# Revit family: Legrand_Bornes_recharge_vehicules_electriques_Green_up_Metal_bornes_recharge_connectees
name_source: partatom
category: Equipement électrique
units: mm (PartAtom-declared; Revit-internal decimal feet)

## family parameters
Basée sur le plan de construction = Non
Configuration du panneau = Deux colonnes, circuits au sein
Cote de connecteur circulaire = Utiliser le diamètre
Couper avec des vides une fois chargée = Non
Numéro OmniClass = 23.80.30.11.17
Partagée = Non
Point de calcul de pièce = Non
Titre OmniClass = Distribution Boards and Control Panels
Toujours verticalement = Oui
Type d'élément = Tableau de raccordement

## types (20) — shared parameters
ETIM Class 6.0 = EC002883
Fabricant = Legrand
IK = 08
IP = 44
Modèle = Borne Métal Green'up Legrand
Tension = 220
URL = www.legrand.fr
déclencheur émission signal de sécurité = 406276
zero-valued in all types: Elévation par défaut

## per-type parameters (varying)
| type | Conditions Générale d'Utilisation | Description | Image du type | Puissance | borne fixation murale | borne sur pied | différentiel | disjoncteur Protection ligne 2P+T (minimum) | disjoncteur différentiel Protection ligne Type 2S | intensité Protection ligne 2P+T | intensité Protection ligne Type 2S | intensité borne | interrupteur différentiel | réglage puissance | section ligne 2P+T  (minimum) | section ligne Type 2S (minimum) |
| Borne Green'up murale Premium monophasée Métal - Mode 3 - 7,4kW - 32A 1 véhicule | https://export.legrand.com | 059004  Borne Green'up murale Premium monophasée Métal - Mode 3 - 7,4kW - 32A 1 véhicule | Borne_ve_metal_murale_059011.jpg | 7.4 | Oui | Non | 30 mA type F (ex Hpi) | 406884 (4500/6 kA) | 410859 (4500/6 kA) | 20 A courbe C | 40 A courbe C | 16 A |  | 7400 W | 3 mm  [stored 0.00984252 ft] | 10 mm  [stored 0.0328084 ft] |
| Borne Green'up murale Premium monophasée Métal - Mode 3 - 4,6kW - 20A 1 véhicule | https://export.legrand.com | 059003  Borne Green'up murale Premium monophasée Métal - Mode 3 - 4,6kW - 20A 1 véhicule | Borne_ve_metal_murale_059011.jpg | 4.6 | Oui | Non | 30 mA type F (ex Hpi) | 406884 (4500/6 kA) | 410755 (4500/6 kA) | 20 A courbe C | 25 A courbe C | 20 A |  | 4600 W | 3 mm  [stored 0.00984252 ft] | 4 mm  [stored 0.0131234 ft] |
| Borne Green'up murale Premium monophasée Métal -  Mode 3 - 3,7kW - 16A 1 véhicule | https://export.legrand.com | 059003  Borne Green'up murale Premium monophasée Métal -  Mode 3 - 3,7kW - 16A 1 véhicule | Borne_ve_metal_murale_059011.jpg | 3.7 | Oui | Non | 30 mA type F (ex Hpi) |  | 410754 (4500/6 kA) |  | 20 A courbe C | 16 A |  | 3700 W | 0 mm  [stored 0 ft] | 3 mm  [stored 0.00984252 ft] |
| Borne Green'up murale Premium triphasée Métal - Mode 3 - 22kW - 32A 1 véhicule | https://export.legrand.com | 059014  Borne Green'up murale Premium triphasée Métal - Mode 3 - 22kW - 32A 1 véhicule | Borne_ve_metal_murale_059011.jpg | 22 | Oui | Non | 30 mA type B | 406884 (4500/6 kA) | 407902 (6000/10 kA) | 20 A courbe C | 40 A courbe C | 32 A | 411846 | 22000 W | 3 mm  [stored 0.00984252 ft] | 10 mm  [stored 0.0328084 ft] |
| Borne Green'up murale Premium monophasée Métal - Modes 2 et 3 - 3,7kW - 16A 1 véhicule | https://export.legrand.com | 059010  Borne Green'up murale Premium monophasée Métal - Modes 2 et 3 - 3,7kW - 16A 1 véhicule | Borne_ve_metal_murale_059011.jpg | 3.7 | Oui | Non | 30 mA type F (ex Hpi) |  | 410754 (4500/6 kA) |  | 20 A courbe C | 20 A |  | 3700 W | 0 mm  [stored 0 ft] | 3 mm  [stored 0.00984252 ft] |
| Borne Green'up murale Premium monophasée Métal - Modes 2 et 3 - 4,6kW - 20A 1 véhicule | https://export.legrand.com | 059010  Borne Green'up murale Premium monophasée Métal - Modes 2 et 3 - 4,6kW - 20A 1 véhicule | Borne_ve_metal_murale_059011.jpg | 4.6 | Oui | Non | 30 mA type F (ex Hpi) | 406884 (4500/6 kA) | 410755 (4500/6 kA) | 20 A courbe C | 25 A courbe C | 20 A |  | 4600 W | 3 mm  [stored 0.00984252 ft] | 4 mm  [stored 0.0131234 ft] |
| Borne Green'up murale Premium monophasée Métal - Modes 2 et 3 - 7,4kW - 32A 1 véhicule | https://export.legrand.com | 059012  Borne Green'up murale Premium monophasée Métal - Modes 2 et 3 - 7,4kW - 32A 1 véhicule | Borne_ve_metal_murale_059011.jpg | 7.4 | Oui | Non | 30 mA type F (ex Hpi) | 406884 (4500/6 kA) | 410859 (4500/6 kA) | 20 A courbe C | 40 A courbe C | 32 A |  | 7400 W | 3 mm  [stored 0.00984252 ft] | 10 mm  [stored 0.0328084 ft] |
| Borne Green'up Premium monophasée Métal -  Mode 3 - 3,7kW - 16A 1 véhicule | https://export.legrand.com 
https://export.legrand.com | 059003 + 059054  Borne Green'up Premium monophasée Métal -  Mode 3 - 3,7kW - 16A 1 véhicule | Borne_ve_metal_pied_059011_059054_pw_231663_pz_3.jpg | 3.7 | Non | Oui | 30 mA type F (ex Hpi) |  | 410754 (4500/6 kA) |  | 20 A courbe C | 16 A |  | 3700 W | 0 mm  [stored 0 ft] | 3 mm  [stored 0.00984252 ft] |
| Borne Green'up Premium monophasée Métal - Mode 3 - 4,6kW - 20A 1 véhicule | https://export.legrand.com | 059003 + 059054  Borne Green'up Premium monophasée Métal - Mode 3 - 4,6kW - 20A 1 véhicule | Borne_ve_metal_pied_059011_059054_pw_231663_pz_3.jpg | 4.6 | Non | Oui | 30 mA type F (ex Hpi) | 406884 (4500/6 kA) | 410755 (4500/6 kA) | 20 A courbe C | 25 A courbe C | 20 A |  | 4600 W | 3 mm  [stored 0.00984252 ft] | 4 mm  [stored 0.0131234 ft] |
| Borne Green'up Premium monophasée Métal - Mode 3 - 7,4kW - 32A 1 véhicule | https://export.legrand.com | 059004 + 059054 - Borne Green'up Premium monophasée Métal - Mode 3 - 7,4kW - 32A 1 véhicule | Borne_ve_metal_murale_059011.jpg | 7.4 | Non | Oui | 30 mA type F (ex Hpi) | 406884 (4500/6 kA) | 410859 (4500/6 kA) | 20 A courbe C | 40 A courbe C | 16 A |  | 7400 W | 3 mm  [stored 0.00984252 ft] | 10 mm  [stored 0.0328084 ft] |
| Borne Green'up Premium monophasée Métal - Modes 2 et 3 - 3,7kW - 16A 1 véhicule | https://export.legrand.com | 059010 + 059054  Borne Green'up Premium monophasée Métal - Modes 2 et 3 - 3,7kW - 16A 1 véhicule | Borne_ve_metal_pied_059011_059054_pw_231663_pz_3.jpg | 3.7 | Non | Oui | 30 mA type F (ex Hpi) |  | 410754 (4500/6 kA) |  | 20 A courbe C | 20 A |  | 3700 W | 0 mm  [stored 0 ft] | 3 mm  [stored 0.00984252 ft] |
| Borne Green'up Premium monophasée Métal - Modes 2 et 3 - 4,6kW - 20A 1 véhicule | https://export.legrand.com | 059010 + 059054  Borne Green'up Premium monophasée Métal - Modes 2 et 3 - 4,6kW - 20A 1 véhicule | Borne_ve_metal_pied_059011_059054_pw_231663_pz_3.jpg | 4.6 | Non | Oui | 30 mA type F (ex Hpi) | 406884 (4500/6 kA) | 410755 (4500/6 kA) | 20 A courbe C | 25 A courbe C | 20 A |  | 4600 W | 3 mm  [stored 0.00984252 ft] | 4 mm  [stored 0.0131234 ft] |
| Borne Green'up Premium monophasée Métal - Modes 2 et 3 - 7,4kW - 32A 1 véhicule | https://export.legrand.com | 059012 + 059054  Borne Green'up Premium monophasée Métal - Modes 2 et 3 - 7,4kW - 32A 1 véhicule | Borne_ve_metal_murale_059011.jpg | 7.4 | Non | Oui | 30 mA type F (ex Hpi) | 406884 (4500/6 kA) | 410859 (4500/6 kA) | 20 A courbe C | 40 A courbe C | 32 A |  | 7400 W | 3 mm  [stored 0.00984252 ft] | 10 mm  [stored 0.0328084 ft] |
| Borne Green'up Premium triphasée Métal - Mode 3 - 22kW - 32A 1 véhicule | https://export.legrand.com | 059014 +059054   Borne Green'up Premium triphasée Métal - Mode 3 - 22kW - 32A 1 véhicule | Borne_ve_metal_pied_059011_059054_pw_231663_pz_3.jpg | 22 | Non | Oui | 30 mA type B | 406884 (4500/6 kA) | 407902 (6000/10 kA) | 20 A courbe C | 40 A courbe C | 32 A | 411846 | 22000 W | 3 mm  [stored 0.00984252 ft] | 10 mm  [stored 0.0328084 ft] |
| Borne Green'up murale Premium monophasée Métal - Modes 2 et 3 - 7,4kW - 32A 2 véhicules | https://export.legrand.com | 059013  Borne Green'up murale Premium monophasée Métal - Modes 2 et 3 - 7,4kW - 32A 2 véhicules | Borne_ve_metal_murale_059011.jpg | 7.4 | Oui | Non | 30 mA type F (ex Hpi) | 406884 (4500/6 kA) | 410859 (4500/6 kA) | 20 A courbe C | 40 A courbe C | 32 A |  | 7400 W | 3 mm  [stored 0.00984252 ft] | 10 mm  [stored 0.0328084 ft] |
| Borne Green'up murale Premium monophasée Métal - Modes 2 et 3 - 3,7kW - 16A 2 véhicules | https://export.legrand.com | 059011  Borne Green'up murale Premium monophasée Métal - Modes 2 et 3 - 3,7kW - 16A 2 véhicules | Borne_ve_metal_murale_059011.jpg | 3.7 | Oui | Non | 30 mA type F (ex Hpi) |  | 410754 (4500/6 kA) |  | 20 A courbe C | 20 A |  | 3700 W | 0 mm  [stored 0 ft] | 3 mm  [stored 0.00984252 ft] |
| Borne Green'up murale Premium monophasée Métal - Modes 2 et 3 - 4,6kW - 20A 2 véhicules | https://export.legrand.com | 059011  Borne Green'up murale Premium monophasée Métal - Modes 2 et 3 - 4,6kW - 20A 2 véhicules | Borne_ve_metal_murale_059011.jpg | 4.6 | Oui | Non | 30 mA type F (ex Hpi) | 406884 (4500/6 kA) | 410755 (4500/6 kA) | 20 A courbe C | 25 A courbe C | 20 A |  | 4600 W | 3 mm  [stored 0.00984252 ft] | 4 mm  [stored 0.0131234 ft] |
| Borne Green'up Premium monophasée Métal - Modes 2 et 3 - 3,7kW - 16A 2 véhicules | https://export.legrand.com | 059011 + 059054  Borne Green'up Premium monophasée Métal - Modes 2 et 3 - 3,7kW - 16A 2 véhicules | Borne_ve_metal_murale_059011.jpg | 3.7 | Oui | Non | 30 mA type F (ex Hpi) |  | 410754 (4500/6 kA) |  | 20 A courbe C | 20 A |  | 3700 W | 0 mm  [stored 0 ft] | 3 mm  [stored 0.00984252 ft] |
| Borne Green'up Premium monophasée Métal - Modes 2 et 3 - 4,6kW - 20A 2 véhicules | https://export.legrand.com | 059011 + 059054  Borne Green'up Premium monophasée Métal - Modes 2 et 3 - 4,6kW - 20A 2 véhicules | Borne_ve_metal_murale_059011.jpg | 4.6 | Oui | Non | 30 mA type F (ex Hpi) | 406884 (4500/6 kA) | 410755 (4500/6 kA) | 20 A courbe C | 25 A courbe C | 20 A |  | 4600 W | 3 mm  [stored 0.00984252 ft] | 4 mm  [stored 0.0131234 ft] |
| Borne Green'up Premium monophasée Métal - Modes 2 et 3 - 7,4kW - 32A 2 véhicules | https://export.legrand.com | 059012 + 059054  Borne Green'up Premium monophasée Métal - Modes 2 et 3 - 7,4kW - 32A 2 véhicules | Borne_ve_metal_murale_059011.jpg | 7.4 | Non | Oui | 30 mA type F (ex Hpi) | 406884 (4500/6 kA) | 410859 (4500/6 kA) | 20 A courbe C | 40 A courbe C | 32 A |  | 7400 W | 3 mm  [stored 0.00984252 ft] | 10 mm  [stored 0.0328084 ft] |

note: [stored X ft] marks values corroborated as IEEE doubles in the binary element streams (Revit-internal decimal feet)
